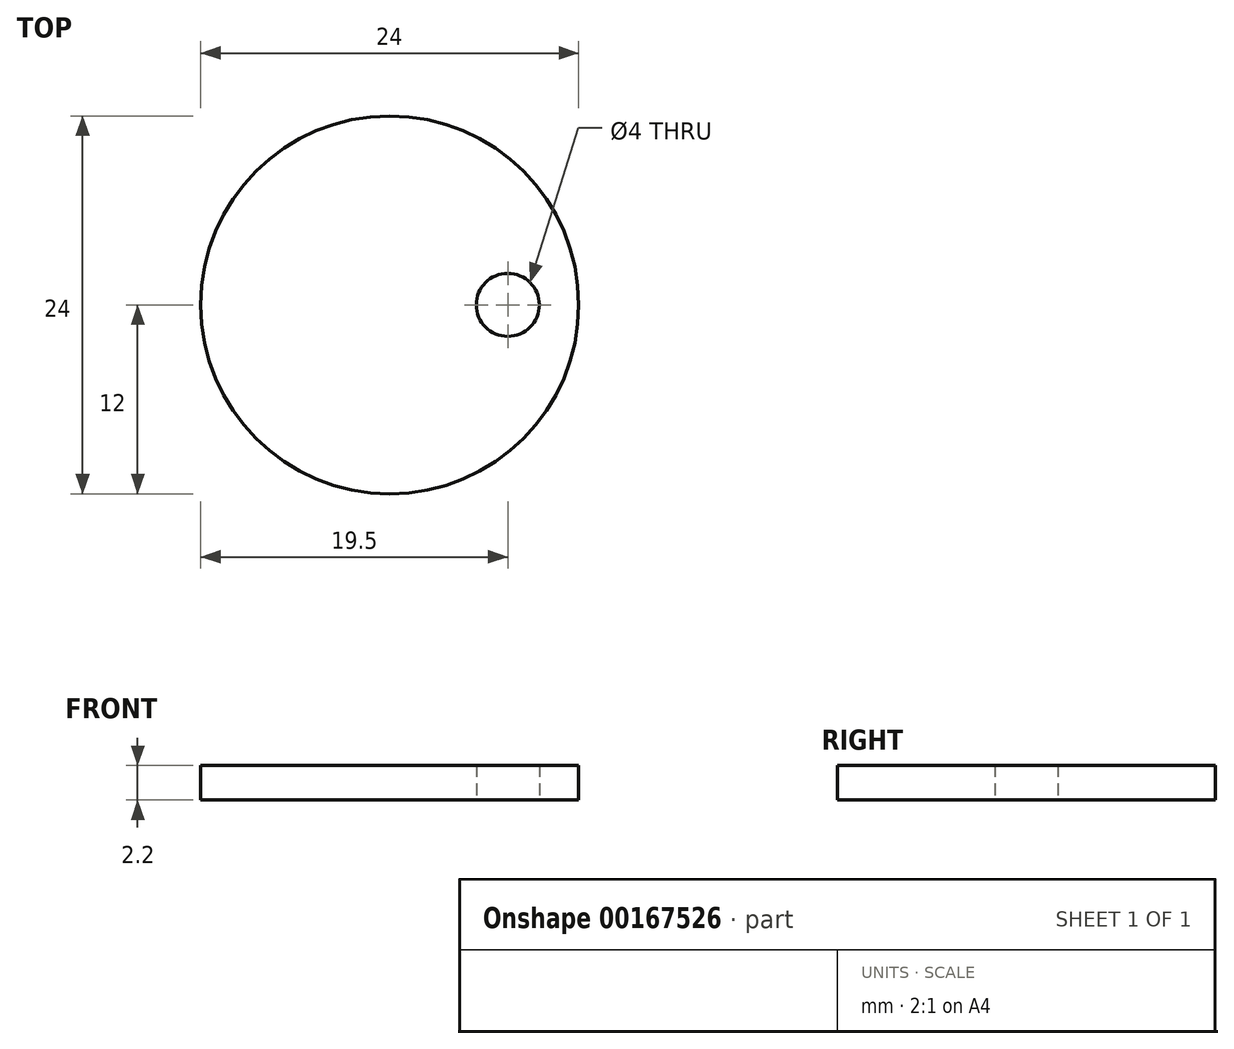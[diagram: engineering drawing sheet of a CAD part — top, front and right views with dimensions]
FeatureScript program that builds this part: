
annotation { "Feature Type Name" : "Feature", "Feature Type Description" : "" }
export const myFeature = defineFeature(function(context is Context, id is Id, definition is map)
    precondition{}
    {
        {
            var Q0;
            Q0=qCreatedBy(makeId("Top.planeOp"),FACE);
            var sketch = newSketch(context, id + "F0", { "sketchPlane" : qUnion([Q0])});
            skLineSegment(sketch, "E0.bottom", {"start": v(-4, 2.5) * mm, "end": v(4, 2.5) * mm});
            skLineSegment(sketch, "E0.top", {"start": v(-4, -2.5) * mm, "end": v(4, -2.5) * mm});
            skLineSegment(sketch, "E0.left", {"start": v(-4, 2.5) * mm, "end": v(-4, -2.5) * mm});
            skLineSegment(sketch, "E0.right", {"start": v(4, 2.5) * mm, "end": v(4, -2.5) * mm});
            skLineSegment(sketch, "E1", {"start": v(-4, -2.5) * mm, "end": v(4, 2.5) * mm, "construction": true});
            skLineSegment(sketch, "E2", {"start": v(0, 0) * mm, "end": v(0, -5) * mm, "construction": true});
            skLineSegment(sketch, "E3", {"start": v(0, -5) * mm, "end": v(-2.5, -2.5) * mm});
            skLineSegment(sketch, "E4.MirrorCS", {"start": v(0, -5) * mm, "end": v(2.5, -2.5) * mm});
            skLineSegment(sketch, "E5.bottom", {"start": v(-1.5, 2.5) * mm, "end": v(1.5, 2.5) * mm, "construction": true});
            skLineSegment(sketch, "E5.top", {"start": v(-1.5, 4.5) * mm, "end": v(1.5, 4.5) * mm, "construction": true});
            skLineSegment(sketch, "E5.left", {"start": v(-1.5, 2.5) * mm, "end": v(-1.5, 4.5) * mm});
            skLineSegment(sketch, "E5.right", {"start": v(1.5, 2.5) * mm, "end": v(1.5, 4.5) * mm});
            skLineSegment(sketch, "E6", {"start": v(0, 4.5) * mm, "end": v(0, 2.5) * mm, "construction": true});
            skLineSegment(sketch, "E7", {"start": v(-4, 2.5) * mm, "end": v(-1.5, 2.5) * mm});
            skLineSegment(sketch, "E8", {"start": v(1.5, 2.5) * mm, "end": v(4, 2.5) * mm});
            skArc(sketch, "E9", {"start": v(5.8, 8.8) * mm, "mid": v(2.76, 7.54) * mm, "end": v(1.5, 4.5) * mm});
            skArc(sketch, "E10.0", {"start": v(5.8, 11.8) * mm, "mid": v(0.64, 9.66) * mm, "end": v(-1.5, 4.5) * mm});
            skLineSegment(sketch, "E11", {"start": v(5.8, 8.8) * mm, "end": v(5.8, 11.8) * mm});
            skSolve(sketch);
        }
        {
            var Q0;
            Q0=makeQuery(id+"F0.imprint","IMPRINT",FACE,{"disambiguationData":[TD([[makeQuery(id+"F0.imprint","IMPRINT",EDGE,{"derivedFrom":sQuery(id+"F0.wireOp",EDGE,"E0.bottom")}),1.0]])]});
            var Q1;
            Q1=makeQuery(id+"F0.imprint","IMPRINT",FACE,{"disambiguationData":[TD([[makeQuery(id+"F0.imprint","IMPRINT",EDGE,{"derivedFrom":sQuery(id+"F0.wireOp",EDGE,"E0.bottom")}),-1.0]])]});
            var Q2;
            {var subQ0=sQuery(id+"F0.wireOp",EDGE,"E3");Q2=makeQuery(id+"F0.imprint","IMPRINT",FACE,{"disambiguationData":[TD([[makeQuery(id+"F0.imprint","IMPRINT",EDGE,{"derivedFrom":subQ0}),-1.0]])]});}
            extrude(context, id + "F1", {"entities" : qUnion([Q0, Q1, Q2]), "depth" : 2.2 * mm});
        }
        {
            var Q0;
            Q0=qCreatedBy(makeId("Top.planeOp"),FACE);
            var sketch = newSketch(context, id + "F2", { "sketchPlane" : qUnion([Q0])});
            skCircle(sketch, "E12", {"center": v(1.5, 3.5) * mm, "radius": 12 * mm});
            skArc(sketch, "E13.0", {"start": v(8.75, 10.39) * mm, "mid": v(-6.17, -2.91) * mm, "end": v(9.56, 9.42) * mm});
            skLineSegment(sketch, "E14.bottom", {"start": v(9.56, 9.42) * mm, "end": v(4.1, 9.42) * mm});
            skLineSegment(sketch, "E14.top", {"start": v(8.75, 10.39) * mm, "end": v(4.1, 10.39) * mm});
            skLineSegment(sketch, "E14.right", {"start": v(4.1, 9.42) * mm, "end": v(4.1, 10.39) * mm});
            skSolve(sketch);
        }
        {
            var Q0;
            Q0=makeQuery(id+"F2.imprint","IMPRINT",FACE,{"disambiguationData":[TD([[makeQuery(id+"F2.imprint","IMPRINT",EDGE,{"derivedFrom":sQuery(id+"F2.wireOp",EDGE,"E12")}),1.0]])]});
            extrude(context, id + "F3", {"entities" : qUnion([Q0]), "operationType" : NewBodyOperationType.ADD, "depth" : 2.2 * mm});
        }
        {
            var Q0;
            Q0=makeQuery(id+"F3.boolean.opBoolean","MERGE",FACE,{"derivedFrom":[makeQuery(id+"F1.opExtrude","CAP_FACE",FACE,{"disambiguationData":[OSD([sQuery(id+"F0.wireOp",EDGE,"E0.top"),sQuery(id+"F0.wireOp",EDGE,"E0.left"),sQuery(id+"F0.wireOp",EDGE,"E0.right"),sQuery(id+"F0.wireOp",EDGE,"E3"),sQuery(id+"F0.wireOp",EDGE,"E4.MirrorCS"),sQuery(id+"F0.wireOp",EDGE,"E5.left"),sQuery(id+"F0.wireOp",EDGE,"E5.right"),sQuery(id+"F0.wireOp",EDGE,"E7"),sQuery(id+"F0.wireOp",EDGE,"E8"),sQuery(id+"F0.wireOp",EDGE,"E9"),sQuery(id+"F0.wireOp",EDGE,"E10.0"),sQuery(id+"F0.wireOp",EDGE,"E11")])],"isStart":false}),makeQuery(id+"F3.opExtrude","CAP_FACE",FACE,{"disambiguationData":[OSD([sQuery(id+"F2.wireOp",EDGE,"E12"),sQuery(id+"F2.wireOp",EDGE,"E13.0"),sQuery(id+"F2.wireOp",EDGE,"E14.bottom"),sQuery(id+"F2.wireOp",EDGE,"E14.top"),sQuery(id+"F2.wireOp",EDGE,"E14.right")])],"isStart":false})]});
            var sketch = newSketch(context, id + "F4", { "sketchPlane" : qUnion([Q0])});
            skArc(sketch, "E15", {"start": v(9.56, 9.42) * mm, "mid": v(8.83, 10.3) * mm, "end": v(8, 11.1) * mm});
            skLineSegment(sketch, "E16.bottom", {"start": v(5.8, 11.1) * mm, "end": v(8, 11.1) * mm});
            skLineSegment(sketch, "E16.top", {"start": v(5.8, 9.42) * mm, "end": v(9.56, 9.42) * mm});
            skLineSegment(sketch, "E16.left", {"start": v(5.8, 11.1) * mm, "end": v(5.8, 9.42) * mm});
            skSolve(sketch);
        }
        {
            var Q0;
            Q0 = qSketchRegion(id + "F4", true);
            extrude(context, id + "F5", {"entities" : qUnion([Q0]), "operationType" : NewBodyOperationType.REMOVE, "oppositeDirection" : true, "depth" : 1 * mm});
        }
        {
            var Q0;
            Q0=makeQuery(id+"F3.boolean.opBoolean","MERGE",FACE,{"derivedFrom":[makeQuery(id+"F1.opExtrude","CAP_FACE",FACE,{"disambiguationData":[OSD([sQuery(id+"F0.wireOp",EDGE,"E0.top"),sQuery(id+"F0.wireOp",EDGE,"E0.left"),sQuery(id+"F0.wireOp",EDGE,"E0.right"),sQuery(id+"F0.wireOp",EDGE,"E3"),sQuery(id+"F0.wireOp",EDGE,"E4.MirrorCS"),sQuery(id+"F0.wireOp",EDGE,"E5.left"),sQuery(id+"F0.wireOp",EDGE,"E5.right"),sQuery(id+"F0.wireOp",EDGE,"E7"),sQuery(id+"F0.wireOp",EDGE,"E8"),sQuery(id+"F0.wireOp",EDGE,"E9"),sQuery(id+"F0.wireOp",EDGE,"E10.0"),sQuery(id+"F0.wireOp",EDGE,"E11")])],"isStart":true}),makeQuery(id+"F3.opExtrude","CAP_FACE",FACE,{"disambiguationData":[OSD([sQuery(id+"F2.wireOp",EDGE,"E12"),sQuery(id+"F2.wireOp",EDGE,"E13.0"),sQuery(id+"F2.wireOp",EDGE,"E14.bottom"),sQuery(id+"F2.wireOp",EDGE,"E14.top"),sQuery(id+"F2.wireOp",EDGE,"E14.right")])],"isStart":true})]});
            var sketch = newSketch(context, id + "F6", { "sketchPlane" : qUnion([Q0])});
            skArc(sketch, "E17", {"start": v(8.75, -10.39) * mm, "mid": v(9.17, -9.91) * mm, "end": v(9.56, -9.42) * mm});
            skLineSegment(sketch, "E18.bottom", {"start": v(5.8, -9.42) * mm, "end": v(9.56, -9.42) * mm});
            skLineSegment(sketch, "E18.top", {"start": v(5.8, -10.39) * mm, "end": v(8.75, -10.39) * mm});
            skLineSegment(sketch, "E18.left", {"start": v(5.8, -9.42) * mm, "end": v(5.8, -10.39) * mm});
            skPoint(sketch, "E18.right.end.orphan", {"position": v(10.16, -10.39) * mm});
            skSolve(sketch);
        }
        {
            var Q0;
            Q0 = qSketchRegion(id + "F6", true);
            extrude(context, id + "F7", {"entities" : qUnion([Q0]), "operationType" : NewBodyOperationType.REMOVE, "oppositeDirection" : true, "depth" : 1 * mm});
        }
        {
            var Q0;
            Q0=qCreatedBy(makeId("Top.planeOp"),FACE);
            var sketch = newSketch(context, id + "F8", { "sketchPlane" : qUnion([Q0])});
            skCircle(sketch, "E19.0", {"center": v(1.5, 3.5) * mm, "radius": 10 * mm});
            skArc(sketch, "E19.1", {"start": v(5.8, 11.8) * mm, "mid": v(0.64, 9.66) * mm, "end": v(-1.5, 4.5) * mm});
            skLineSegment(sketch, "E19.2", {"start": v(-1.5, 2.5) * mm, "end": v(-1.5, 4.5) * mm});
            skLineSegment(sketch, "E19.3", {"start": v(-4, 2.5) * mm, "end": v(-1.5, 2.5) * mm});
            skLineSegment(sketch, "E19.4", {"start": v(-4, 2.5) * mm, "end": v(-4, -2.5) * mm});
            skLineSegment(sketch, "E19.5", {"start": v(-4, -2.5) * mm, "end": v(-2.5, -2.5) * mm});
            skLineSegment(sketch, "E19.6", {"start": v(0, -5) * mm, "end": v(-2.5, -2.5) * mm});
            skLineSegment(sketch, "E19.7", {"start": v(0, -5) * mm, "end": v(2.5, -2.5) * mm});
            skLineSegment(sketch, "E19.8", {"start": v(2.5, -2.5) * mm, "end": v(4, -2.5) * mm});
            skLineSegment(sketch, "E19.9", {"start": v(4, 2.5) * mm, "end": v(4, -2.5) * mm});
            skLineSegment(sketch, "E19.10", {"start": v(1.5, 2.5) * mm, "end": v(4, 2.5) * mm});
            skLineSegment(sketch, "E19.11", {"start": v(1.5, 2.5) * mm, "end": v(1.5, 4.5) * mm});
            skArc(sketch, "E19.12", {"start": v(5.8, 8.8) * mm, "mid": v(2.76, 7.54) * mm, "end": v(1.5, 4.5) * mm});
            skLineSegment(sketch, "E19.13", {"start": v(5.8, 8.8) * mm, "end": v(5.8, 11.8) * mm});
            skCircle(sketch, "E20", {"center": v(9, 3.5) * mm, "radius": 2 * mm});
            skSolve(sketch);
        }
        {
            var Q0;
            Q0=makeQuery(id+"F8.imprint","IMPRINT",FACE,{"disambiguationData":[TD([[makeQuery(id+"F8.imprint","IMPRINT",EDGE,{"derivedFrom":sQuery(id+"F8.wireOp",EDGE,"E19.0")}),1.0]])]});
            extrude(context, id + "F9", {"entities" : qUnion([Q0]), "depth" : 2.2 * mm});
        }
        {
            var Q0;
            Q0=makeQuery(id+"F9.opExtrude","CAP_FACE",FACE,{"disambiguationData":[OSD([sQuery(id+"F8.wireOp",EDGE,"E19.0"),sQuery(id+"F8.wireOp",EDGE,"E19.1"),sQuery(id+"F8.wireOp",EDGE,"E19.2"),sQuery(id+"F8.wireOp",EDGE,"E19.3"),sQuery(id+"F8.wireOp",EDGE,"E19.4"),sQuery(id+"F8.wireOp",EDGE,"E19.5"),sQuery(id+"F8.wireOp",EDGE,"E19.6"),sQuery(id+"F8.wireOp",EDGE,"E19.7"),sQuery(id+"F8.wireOp",EDGE,"E19.8"),sQuery(id+"F8.wireOp",EDGE,"E19.9"),sQuery(id+"F8.wireOp",EDGE,"E19.10"),sQuery(id+"F8.wireOp",EDGE,"E19.11"),sQuery(id+"F8.wireOp",EDGE,"E19.12"),sQuery(id+"F8.wireOp",EDGE,"E19.13"),sQuery(id+"F8.wireOp",EDGE,"E20")])],"isStart":true});
            var sketch = newSketch(context, id + "F10", { "sketchPlane" : qUnion([Q0])});
            skCircle(sketch, "E21", {"center": v(1.5, -3.5) * mm, "radius": 10 * mm});
            skSolve(sketch);
        }
        {
            var Q0;
            Q0=makeQuery(id+"F10.imprint","IMPRINT",FACE,{"disambiguationData":[TD([[makeQuery(id+"F10.imprint","IMPRINT",EDGE,{"derivedFrom":sQuery(id+"F10.wireOp",EDGE,"E21")}),-1.0]])]});
            var Q1;
            Q1=sQuery(id+"F10.wireOp",EDGE,"E21");
            extrude(context, id + "F11", {"entities" : qUnion([Q0]), "operationType" : NewBodyOperationType.REMOVE, "surfaceEntities" : qUnion([Q1]), "oppositeDirection" : true, "depth" : 1.1 * mm});
        }
        {
            var Q0;
            Q0=makeQuery(id+"F1.opExtrude","CAP_FACE",FACE,{"disambiguationData":[OSD([sQuery(id+"F0.wireOp",EDGE,"E0.top"),sQuery(id+"F0.wireOp",EDGE,"E0.left"),sQuery(id+"F0.wireOp",EDGE,"E0.right"),sQuery(id+"F0.wireOp",EDGE,"E3"),sQuery(id+"F0.wireOp",EDGE,"E4.MirrorCS"),sQuery(id+"F0.wireOp",EDGE,"E5.left"),sQuery(id+"F0.wireOp",EDGE,"E5.right"),sQuery(id+"F0.wireOp",EDGE,"E7"),sQuery(id+"F0.wireOp",EDGE,"E8"),sQuery(id+"F0.wireOp",EDGE,"E9"),sQuery(id+"F0.wireOp",EDGE,"E10.0"),sQuery(id+"F0.wireOp",EDGE,"E11")])],"isStart":true});
            var sketch = newSketch(context, id + "F12", { "sketchPlane" : qUnion([Q0])});
            skCircle(sketch, "E22", {"center": v(1.5, -3.5) * mm, "radius": 10 * mm});
            skSolve(sketch);
        }
        {
            var Q0;
            Q0 = qSketchRegion(id + "F12", true);
            extrude(context, id + "F13", {"entities" : qUnion([Q0]), "operationType" : NewBodyOperationType.REMOVE, "oppositeDirection" : true, "depth" : 1.1 * mm});
        }
        {
            var Q0;
            Q0=makeQuery(id+"F11.boolean.opBoolean","COPY",FACE,{"derivedFrom":makeQuery(id+"F11.opExtrude","CAP_FACE",FACE,{"disambiguationData":[OSD([sQuery(id+"F8.wireOp",EDGE,"E19.1"),sQuery(id+"F8.wireOp",EDGE,"E19.2"),sQuery(id+"F8.wireOp",EDGE,"E19.3"),sQuery(id+"F8.wireOp",EDGE,"E19.4"),sQuery(id+"F8.wireOp",EDGE,"E19.5"),sQuery(id+"F8.wireOp",EDGE,"E19.6"),sQuery(id+"F8.wireOp",EDGE,"E19.7"),sQuery(id+"F8.wireOp",EDGE,"E19.8"),sQuery(id+"F8.wireOp",EDGE,"E19.9"),sQuery(id+"F8.wireOp",EDGE,"E19.10"),sQuery(id+"F8.wireOp",EDGE,"E19.11"),sQuery(id+"F8.wireOp",EDGE,"E19.12"),sQuery(id+"F8.wireOp",EDGE,"E19.13"),sQuery(id+"F8.wireOp",EDGE,"E20"),sQuery(id+"F10.wireOp",EDGE,"E21")])],"isStart":false})});
            var sketch = newSketch(context, id + "F14", { "sketchPlane" : qUnion([Q0])});
            skLineSegment(sketch, "E23.bottom", {"start": v(-4, -4.5) * mm, "end": v(4, -4.5) * mm});
            skLineSegment(sketch, "E23.top", {"start": v(-4, -9.5) * mm, "end": v(4, -9.5) * mm});
            skLineSegment(sketch, "E23.left", {"start": v(-4, -4.5) * mm, "end": v(-4, -9.5) * mm});
            skLineSegment(sketch, "E23.right", {"start": v(4, -4.5) * mm, "end": v(4, -9.5) * mm});
            skLineSegment(sketch, "E24", {"start": v(-4, -9.5) * mm, "end": v(4, -4.5) * mm, "construction": true});
            skLineSegment(sketch, "E25", {"start": v(0, -7) * mm, "end": v(0, -12) * mm, "construction": true});
            skLineSegment(sketch, "E26", {"start": v(0, -12) * mm, "end": v(-2.5, -9.5) * mm});
            skLineSegment(sketch, "E27.MirrorCS", {"start": v(0, -12) * mm, "end": v(2.5, -9.5) * mm});
            skLineSegment(sketch, "E28.bottom", {"start": v(-1.5, -4.5) * mm, "end": v(1.5, -4.5) * mm, "construction": true});
            skLineSegment(sketch, "E28.top", {"start": v(-1.5, -2.5) * mm, "end": v(1.5, -2.5) * mm, "construction": true});
            skLineSegment(sketch, "E28.left", {"start": v(-1.5, -4.5) * mm, "end": v(-1.5, -2.5) * mm});
            skLineSegment(sketch, "E28.right", {"start": v(1.5, -4.5) * mm, "end": v(1.5, -2.5) * mm});
            skLineSegment(sketch, "E29", {"start": v(0, -2.5) * mm, "end": v(0, -4.5) * mm, "construction": true});
            skLineSegment(sketch, "E30", {"start": v(-4, -4.5) * mm, "end": v(-1.5, -4.5) * mm});
            skLineSegment(sketch, "E31", {"start": v(1.5, -4.5) * mm, "end": v(4, -4.5) * mm});
            skArc(sketch, "E32", {"start": v(5.8, 1.8) * mm, "mid": v(2.76, 0.54) * mm, "end": v(1.5, -2.5) * mm});
            skArc(sketch, "E33.0", {"start": v(5.8, 4.8) * mm, "mid": v(0.64, 2.66) * mm, "end": v(-1.5, -2.5) * mm});
            skLineSegment(sketch, "E34", {"start": v(5.8, 1.8) * mm, "end": v(5.8, 4.8) * mm});
            skSolve(sketch);
        }
        {
            var Q0;
            Q0 = qSketchRegion(id + "F14", true);
            extrude(context, id + "F15", {"entities" : qUnion([Q0]), "operationType" : NewBodyOperationType.ADD, "depth" : 1.1 * mm});
        }
        {
            var Q0;
            Q0=makeQuery(id+"F11.boolean.opBoolean","COPY",FACE,{"derivedFrom":makeQuery(id+"F11.opExtrude","CAP_FACE",FACE,{"disambiguationData":[OSD([sQuery(id+"F8.wireOp",EDGE,"E19.1"),sQuery(id+"F8.wireOp",EDGE,"E19.2"),sQuery(id+"F8.wireOp",EDGE,"E19.3"),sQuery(id+"F8.wireOp",EDGE,"E19.4"),sQuery(id+"F8.wireOp",EDGE,"E19.5"),sQuery(id+"F8.wireOp",EDGE,"E19.6"),sQuery(id+"F8.wireOp",EDGE,"E19.7"),sQuery(id+"F8.wireOp",EDGE,"E19.8"),sQuery(id+"F8.wireOp",EDGE,"E19.9"),sQuery(id+"F8.wireOp",EDGE,"E19.10"),sQuery(id+"F8.wireOp",EDGE,"E19.11"),sQuery(id+"F8.wireOp",EDGE,"E19.12"),sQuery(id+"F8.wireOp",EDGE,"E19.13"),sQuery(id+"F8.wireOp",EDGE,"E20"),sQuery(id+"F10.wireOp",EDGE,"E21")])],"isStart":false})});
            var sketch = newSketch(context, id + "F16", { "sketchPlane" : qUnion([Q0])});
            skCircle(sketch, "E35.0", {"center": v(1.5, -3.5) * mm, "radius": 10 * mm});
            skLineSegment(sketch, "E35.1", {"start": v(4, -4.5) * mm, "end": v(4, -9.5) * mm});
            skLineSegment(sketch, "E35.2", {"start": v(2.5, -9.5) * mm, "end": v(4, -9.5) * mm});
            skLineSegment(sketch, "E35.3", {"start": v(0, -12) * mm, "end": v(2.5, -9.5) * mm});
            skLineSegment(sketch, "E35.4", {"start": v(0, -12) * mm, "end": v(-2.5, -9.5) * mm});
            skLineSegment(sketch, "E35.5", {"start": v(-4, -9.5) * mm, "end": v(-2.5, -9.5) * mm});
            skLineSegment(sketch, "E35.6", {"start": v(-4, -4.5) * mm, "end": v(-4, -9.5) * mm});
            skLineSegment(sketch, "E35.7", {"start": v(-4, -4.5) * mm, "end": v(-1.5, -4.5) * mm});
            skLineSegment(sketch, "E35.8", {"start": v(1.5, -4.5) * mm, "end": v(4, -4.5) * mm});
            skLineSegment(sketch, "E35.9", {"start": v(1.5, -4.5) * mm, "end": v(1.5, -2.5) * mm});
            skLineSegment(sketch, "E35.10", {"start": v(-1.5, -4.5) * mm, "end": v(-1.5, -2.5) * mm});
            skArc(sketch, "E35.11", {"start": v(5.8, 4.8) * mm, "mid": v(0.64, 2.66) * mm, "end": v(-1.5, -2.5) * mm});
            skArc(sketch, "E35.12", {"start": v(5.8, 1.8) * mm, "mid": v(2.76, 0.54) * mm, "end": v(1.5, -2.5) * mm});
            skLineSegment(sketch, "E35.13", {"start": v(5.8, 1.8) * mm, "end": v(5.8, 4.8) * mm});
            skCircle(sketch, "E36.0", {"center": v(9, -3.5) * mm, "radius": 2 * mm});
            skSolve(sketch);
        }
        {
            var Q0;
            Q0 = qSketchRegion(id + "F16", true);
            extrude(context, id + "F17", {"entities" : qUnion([Q0]), "operationType" : NewBodyOperationType.ADD, "depth" : 1.1 * mm});
        }
    });
